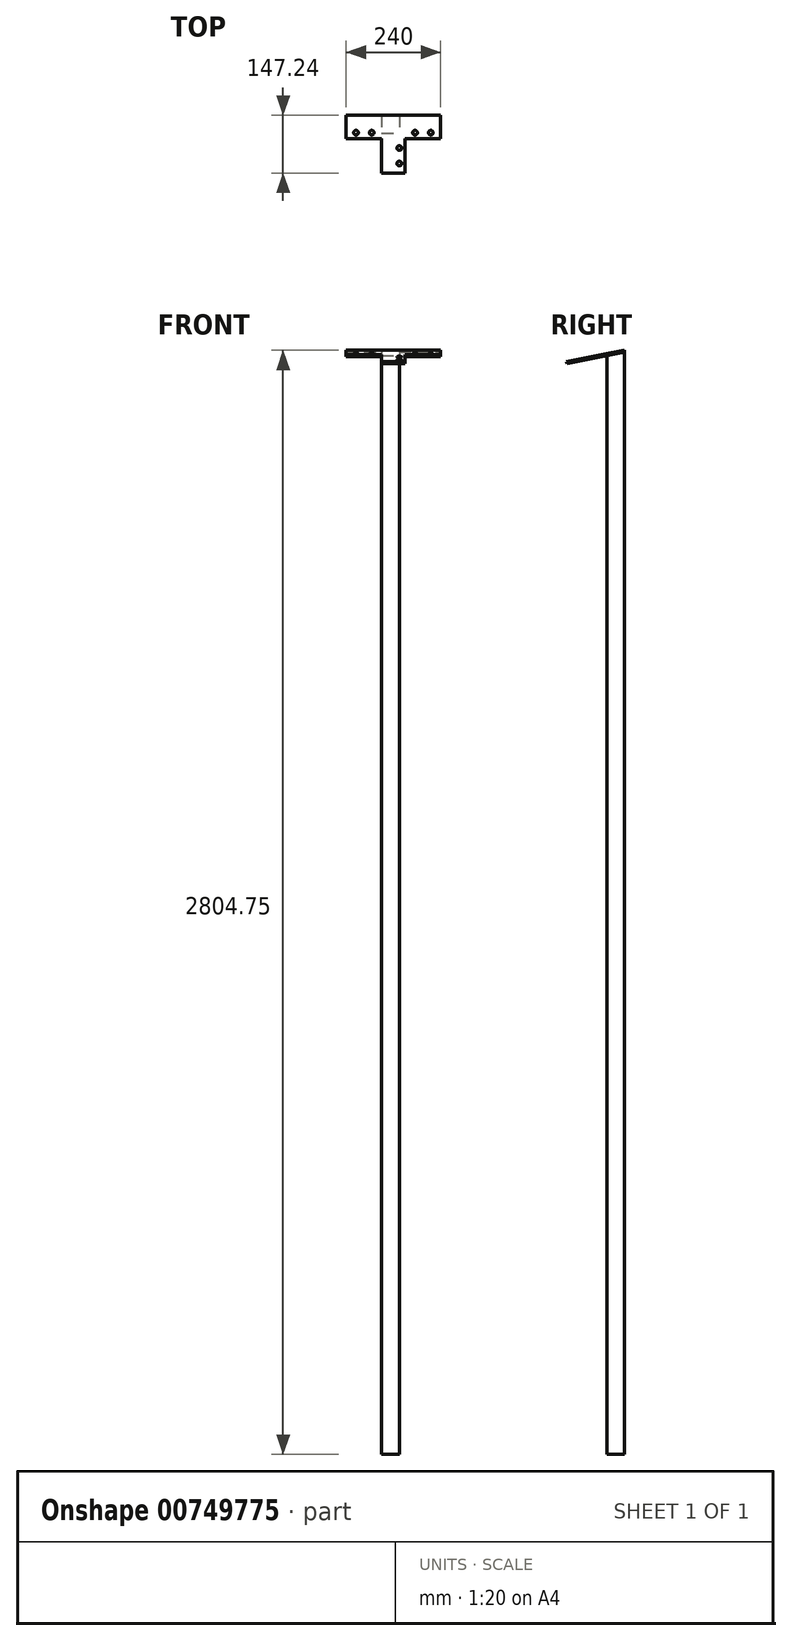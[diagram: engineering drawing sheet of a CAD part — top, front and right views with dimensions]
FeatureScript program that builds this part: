
annotation { "Feature Type Name" : "Feature", "Feature Type Description" : "" }
export const myFeature = defineFeature(function(context is Context, id is Id, definition is map)
    precondition{}
    {
        {
            var Q0;
            Q0=qCreatedBy(makeId("Top.planeOp"),FACE);
            var sketch = newSketch(context, id + "F0", { "sketchPlane" : qUnion([Q0])});
            skLineSegment(sketch, "E0.bottom", {"start": v(22.5, -22.5) * mm, "end": v(-22.5, -22.5) * mm});
            skLineSegment(sketch, "E0.top", {"start": v(22.5, 22.5) * mm, "end": v(-22.5, 22.5) * mm});
            skLineSegment(sketch, "E0.left", {"start": v(22.5, -22.5) * mm, "end": v(22.5, 22.5) * mm});
            skLineSegment(sketch, "E0.right", {"start": v(-22.5, -22.5) * mm, "end": v(-22.5, 22.5) * mm});
            skPoint(sketch, "E0.middle", {"position": v(0, 0) * mm});
            skSolve(sketch);
        }
        {
            var Q0;
            Q0=qSketchRegion(id+"F0",true);
            extrude(context, id + "F1", {"entities" : qUnion([Q0]), "depth" : 3330 * mm, "offsetDistance" : 25 * mm});
        }
        {
            var Q0;
            Q0=qCreatedBy(makeId("Top.planeOp"),FACE);
            cPlane(context, id + "F2", {"entities" : qUnion([Q0]), "cplaneType" : CPlaneType.OFFSET, "offset" : 965 * mm, "width" : 150 * mm, "height" : 150 * mm});
        }
        {
            var Q0;
            Q0=qCreatedBy(id+"F2.planeOp",FACE);
            var sketch = newSketch(context, id + "F3", { "sketchPlane" : qUnion([Q0])});
            skLineSegment(sketch, "E1", {"start": v(0, 0) * mm, "end": v(22.5, 0) * mm});
            skLineSegment(sketch, "E2", {"start": v(22.5, 0) * mm, "end": v(32.5, 0) * mm});
            skCircle(sketch, "E3", {"center": v(32.5, 0) * mm, "radius": 10 * mm});
            skLineSegment(sketch, "E4", {"start": v(32.5, 0) * mm, "end": v(32.5, 2) * mm});
            skLineSegment(sketch, "E5", {"start": v(32.5, 0) * mm, "end": v(32.5, -2) * mm});
            skLineSegment(sketch, "E6", {"start": v(32.5, -2) * mm, "end": v(22.5, -2) * mm});
            skLineSegment(sketch, "E7", {"start": v(32.5, 2) * mm, "end": v(22.5, 2) * mm});
            skLineSegment(sketch, "E8", {"start": v(0, 0) * mm, "end": v(-22.5, 0) * mm});
            skLineSegment(sketch, "E9", {"start": v(-22.5, 0) * mm, "end": v(-32.5, 0) * mm});
            skCircle(sketch, "E10", {"center": v(-32.5, 0) * mm, "radius": 10 * mm});
            skSolve(sketch);
        }
        {
            var Q0;
            Q0=makeQuery(id+"F1.opExtrude","CAP_EDGE",EDGE,{"disambiguationData":[OSD([sQuery(id+"F0.wireOp",EDGE,"E0.bottom")])],"isStart":false});
            cPlane(context, id + "F4", {"entities" : qUnion([Q0]), "cplaneType" : CPlaneType.LINE_ANGLE, "offset" : 25 * mm, "angle" : 101 * degree, "oppositeDirection" : true, "width" : 150 * mm, "height" : 150 * mm});
        }
        {
            var Q0;
            Q0=makeQuery(id+"F1.opExtrude","CAP_FACE",FACE,{"disambiguationData":[OSD([sQuery(id+"F0.wireOp",EDGE,"E0.bottom"),sQuery(id+"F0.wireOp",EDGE,"E0.top"),sQuery(id+"F0.wireOp",EDGE,"E0.left"),sQuery(id+"F0.wireOp",EDGE,"E0.right")])],"isStart":false});
            var sketch = newSketch(context, id + "F5", { "sketchPlane" : qUnion([Q0])});
            skLineSegment(sketch, "E11.bottom", {"start": v(-22.5, 22.5) * mm, "end": v(22.5, 22.5) * mm});
            skLineSegment(sketch, "E11.top", {"start": v(-22.5, -22.5) * mm, "end": v(22.5, -22.5) * mm});
            skLineSegment(sketch, "E11.left", {"start": v(-22.5, 22.5) * mm, "end": v(-22.5, -22.5) * mm});
            skLineSegment(sketch, "E11.right", {"start": v(22.5, 22.5) * mm, "end": v(22.5, -22.5) * mm});
            skSolve(sketch);
        }
        {
            var Q0;
            Q0=qCreatedBy(id+"F4.planeOp",FACE);
            var sketch = newSketch(context, id + "F6", { "sketchPlane" : qUnion([Q0])});
            skLineSegment(sketch, "E12.bottom", {"start": v(-22.5, -659.15) * mm, "end": v(22.5, -659.15) * mm});
            skLineSegment(sketch, "E12.top", {"start": v(-22.5, -613.3) * mm, "end": v(22.5, -613.3) * mm});
            skLineSegment(sketch, "E12.left", {"start": v(-22.5, -659.15) * mm, "end": v(-22.5, -613.3) * mm});
            skLineSegment(sketch, "E12.right", {"start": v(22.5, -659.15) * mm, "end": v(22.5, -613.3) * mm});
            skSolve(sketch);
        }
        {
            var Q0;
            Q0=makeQuery(id+"F6.imprint","IMPRINT",FACE,{"disambiguationData":[TD([[makeQuery(id+"F6.imprint","IMPRINT",EDGE,{"derivedFrom":sQuery(id+"F6.wireOp",EDGE,"E12.bottom")}),1.0]])]});
            extrude(context, id + "F7", {"entities" : qUnion([Q0]), "operationType" : NewBodyOperationType.ADD, "depth" : 25 * mm, "offsetDistance" : 25 * mm});
        }
        {
            var Q0;
            Q0=qCreatedBy(id+"F4.planeOp",FACE);
            var sketch = newSketch(context, id + "F8", { "sketchPlane" : qUnion([Q0])});
            skLineSegment(sketch, "E13.bottom", {"start": v(-22.5, -659.15) * mm, "end": v(37.5, -659.15) * mm});
            skLineSegment(sketch, "E13.top", {"start": v(-22.5, -599.15) * mm, "end": v(37.5, -599.15) * mm});
            skLineSegment(sketch, "E13.left", {"start": v(-22.5, -659.15) * mm, "end": v(-22.5, -599.15) * mm});
            skLineSegment(sketch, "E13.right", {"start": v(37.5, -659.15) * mm, "end": v(37.5, -599.15) * mm});
            skLineSegment(sketch, "E14.bottom", {"start": v(37.5, -659.15) * mm, "end": v(127.5, -659.15) * mm});
            skLineSegment(sketch, "E14.top", {"start": v(37.5, -599.15) * mm, "end": v(127.5, -599.15) * mm});
            skLineSegment(sketch, "E14.right", {"start": v(127.5, -659.15) * mm, "end": v(127.5, -599.15) * mm});
            skLineSegment(sketch, "E15.top", {"start": v(-22.5, -509.15) * mm, "end": v(37.5, -509.15) * mm});
            skLineSegment(sketch, "E15.left", {"start": v(-22.5, -599.15) * mm, "end": v(-22.5, -509.15) * mm});
            skLineSegment(sketch, "E15.right", {"start": v(37.5, -599.15) * mm, "end": v(37.5, -509.15) * mm});
            skLineSegment(sketch, "E16", {"start": v(-22.5, -659.15) * mm, "end": v(-22.5, -509.15) * mm});
            skLineSegment(sketch, "E17", {"start": v(-22.5, -659.15) * mm, "end": v(-112.5, -659.15) * mm});
            skLineSegment(sketch, "E18", {"start": v(-112.5, -659.15) * mm, "end": v(-112.5, -599.15) * mm});
            skLineSegment(sketch, "E19", {"start": v(-112.5, -599.15) * mm, "end": v(-22.5, -599.15) * mm});
            skSolve(sketch);
        }
        {
            var Q0;
            Q0=qSketchRegion(id+"F8",true);
            extrude(context, id + "F9", {"entities" : qUnion([Q0]), "operationType" : NewBodyOperationType.ADD, "depth" : 5 * mm, "offsetDistance" : 25 * mm});
        }
        {
            var Q0;
            Q0=makeQuery(id+"F9.boolean.opBoolean","MERGE",FACE,{"derivedFrom":[makeQuery(id+"F7.opExtrude","CAP_FACE",FACE,{"disambiguationData":[OSD([sQuery(id+"F6.wireOp",EDGE,"E12.bottom"),sQuery(id+"F6.wireOp",EDGE,"E12.top"),sQuery(id+"F6.wireOp",EDGE,"E12.left"),sQuery(id+"F6.wireOp",EDGE,"E12.right")])],"isStart":true}),makeQuery(id+"F9.opExtrude","CAP_FACE",FACE,{"disambiguationData":[OSD([sQuery(id+"F8.wireOp",EDGE,"E13.bottom"),sQuery(id+"F8.wireOp",EDGE,"E14.bottom"),sQuery(id+"F8.wireOp",EDGE,"E14.top"),sQuery(id+"F8.wireOp",EDGE,"E14.right"),sQuery(id+"F8.wireOp",EDGE,"E15.top"),sQuery(id+"F8.wireOp",EDGE,"E15.right"),sQuery(id+"F8.wireOp",EDGE,"E16")])],"isStart":true})]});
            var sketch = newSketch(context, id + "F10", { "sketchPlane" : qUnion([Q0])});
            skLineSegment(sketch, "E20", {"start": v(37.5, 509.15) * mm, "end": v(37.5, 534.15) * mm});
            skLineSegment(sketch, "E21", {"start": v(37.5, 534.15) * mm, "end": v(22.5, 534.15) * mm});
            skLineSegment(sketch, "E22", {"start": v(22.5, 534.15) * mm, "end": v(22.5, 574.15) * mm});
            skLineSegment(sketch, "E23", {"start": v(127.5, 599.15) * mm, "end": v(102.5, 599.15) * mm});
            skLineSegment(sketch, "E24", {"start": v(102.5, 599.15) * mm, "end": v(102.5, 614.15) * mm});
            skLineSegment(sketch, "E25", {"start": v(102.5, 614.15) * mm, "end": v(62.5, 614.15) * mm});
            skCircle(sketch, "E26", {"center": v(102.5, 614.15) * mm, "radius": 6 * mm});
            skCircle(sketch, "E27", {"center": v(62.5, 614.15) * mm, "radius": 6 * mm});
            skLineSegment(sketch, "E28", {"start": v(7.5, 509.15) * mm, "end": v(7.5, 602.33) * mm});
            skCircle(sketch, "E29.MirrorC", {"center": v(-47.5, 614.15) * mm, "radius": 6 * mm});
            skCircle(sketch, "E30.MirrorC", {"center": v(-87.5, 614.15) * mm, "radius": 6 * mm});
            skCircle(sketch, "E31.MirrorC", {"center": v(22.5, 534.15) * mm, "radius": 6 * mm});
            skCircle(sketch, "E32.MirrorC", {"center": v(22.5, 574.15) * mm, "radius": 6 * mm});
            skSolve(sketch);
        }
        {
            var Q0;
            Q0=qSketchRegion(id+"F10",true);
            extrude(context, id + "F11", {"entities" : qUnion([Q0]), "operationType" : NewBodyOperationType.REMOVE, "oppositeDirection" : true, "depth" : 25 * mm, "offsetDistance" : 25 * mm});
        }
        {
            var Q0;
            Q0=qCreatedBy(makeId("Top.planeOp"),FACE);
            var sketch = newSketch(context, id + "F12", { "sketchPlane" : qUnion([Q0])});
            skLineSegment(sketch, "E33.bottom", {"start": v(-22.5, 22.5) * mm, "end": v(127.5, 22.5) * mm});
            skLineSegment(sketch, "E33.top", {"start": v(-22.5, 27.27) * mm, "end": v(127.5, 27.27) * mm});
            skLineSegment(sketch, "E33.left", {"start": v(-22.5, 22.5) * mm, "end": v(-22.5, 27.27) * mm});
            skLineSegment(sketch, "E33.right", {"start": v(127.5, 22.5) * mm, "end": v(127.5, 27.27) * mm});
            skSolve(sketch);
        }
        {
            var Q0;
            Q0=qSketchRegion(id+"F12",true);
            extrude(context, id + "F13", {"entities" : qUnion([Q0]), "operationType" : NewBodyOperationType.REMOVE, "depth" : 3358.7 * mm, "offsetDistance" : 25 * mm});
        }
        {
            var Q0;
            Q0=makeQuery(id+"F13.boolean.opBoolean","COPY",FACE,{"derivedFrom":makeQuery(id+"F13.opExtrude","SWEPT_FACE",FACE,{"disambiguationData":[OSD([sQuery(id+"F12.wireOp",EDGE,"E33.left")])]})});
            var sketch = newSketch(context, id + "F14", { "sketchPlane" : qUnion([Q0])});
            skLineSegment(sketch, "E34", {"start": v(23.45, 3333.84) * mm, "end": v(22.5, 3333.65) * mm});
            skLineSegment(sketch, "E35", {"start": v(22.5, 3333.65) * mm, "end": v(22.5, 3338.75) * mm});
            skLineSegment(sketch, "E36", {"start": v(22.5, 3338.75) * mm, "end": v(23.45, 3333.84) * mm});
            skSolve(sketch);
        }
        {
            var Q0;
            Q0=qSketchRegion(id+"F14",true);
            extrude(context, id + "F15", {"entities" : qUnion([Q0]), "operationType" : NewBodyOperationType.REMOVE, "oppositeDirection" : true, "depth" : 111 * mm, "offsetDistance" : 25 * mm});
        }
        {
            var Q0;
            Q0=makeQuery(id+"F1.opExtrude","CAP_FACE",FACE,{"disambiguationData":[OSD([sQuery(id+"F0.wireOp",EDGE,"E0.bottom"),sQuery(id+"F0.wireOp",EDGE,"E0.top"),sQuery(id+"F0.wireOp",EDGE,"E0.left"),sQuery(id+"F0.wireOp",EDGE,"E0.right")])],"isStart":true});
            var sketch = newSketch(context, id + "F16", { "sketchPlane" : qUnion([Q0])});
            skLineSegment(sketch, "E37.bottom", {"start": v(-22.5, 22.5) * mm, "end": v(22.5, 22.5) * mm});
            skLineSegment(sketch, "E37.top", {"start": v(-22.5, -22.5) * mm, "end": v(22.5, -22.5) * mm});
            skLineSegment(sketch, "E37.left", {"start": v(-22.5, 22.5) * mm, "end": v(-22.5, -22.5) * mm});
            skLineSegment(sketch, "E37.right", {"start": v(22.5, 22.5) * mm, "end": v(22.5, -22.5) * mm});
            skSolve(sketch);
        }
        {
            var Q0;
            Q0 = qSketchRegion(id + "F16", true);
            extrude(context, id + "F17", {"entities" : qUnion([Q0]), "operationType" : NewBodyOperationType.REMOVE, "oppositeDirection" : true, "depth" : 534 * mm, "offsetDistance" : 25 * mm});
        }
    });
